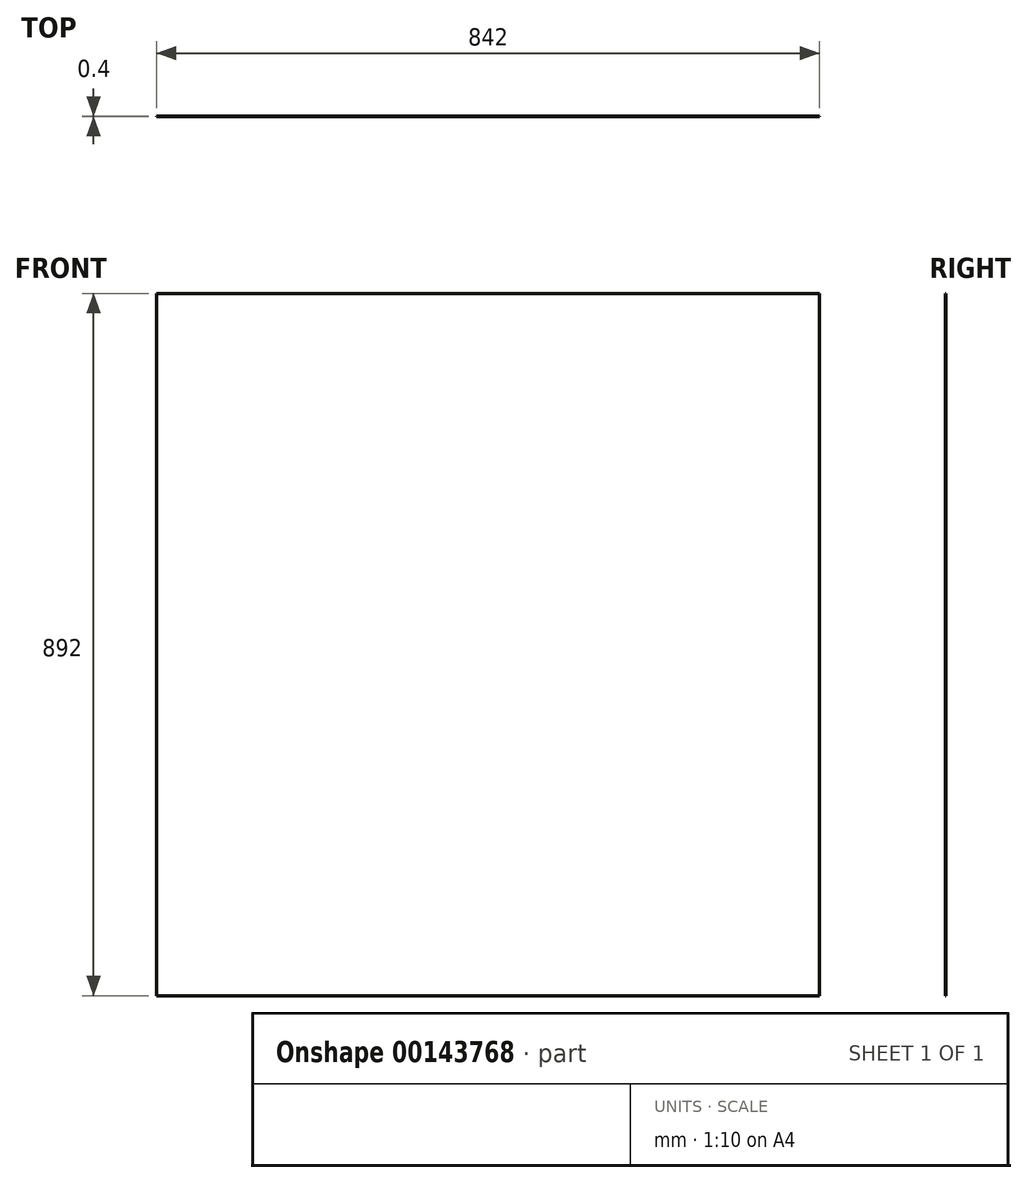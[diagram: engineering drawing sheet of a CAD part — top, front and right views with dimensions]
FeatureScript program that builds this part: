
annotation { "Feature Type Name" : "Feature", "Feature Type Description" : "" }
export const myFeature = defineFeature(function(context is Context, id is Id, definition is map)
    precondition{}
    {
        {
            var Q0;
            Q0=qCreatedBy(makeId("Front.planeOp"),FACE);
            var sketch = newSketch(context, id + "F0", { "sketchPlane" : qUnion([Q0])});
            skLineSegment(sketch, "E0", {"start": v(-421, 446) * mm, "end": v(421, 446) * mm});
            skLineSegment(sketch, "E1", {"start": v(421, 446) * mm, "end": v(421, -446) * mm});
            skLineSegment(sketch, "E2", {"start": v(421, -446) * mm, "end": v(-421, -446) * mm});
            skLineSegment(sketch, "E3", {"start": v(-421, -446) * mm, "end": v(-421, 446) * mm});
            skSolve(sketch);
        }
        {
            var Q0;
            Q0 = qSketchRegion(id + "F0", true);
            extrude(context, id + "F1", {"entities" : qUnion([Q0]), "depth" : 0.4 * mm});
        }
    });
